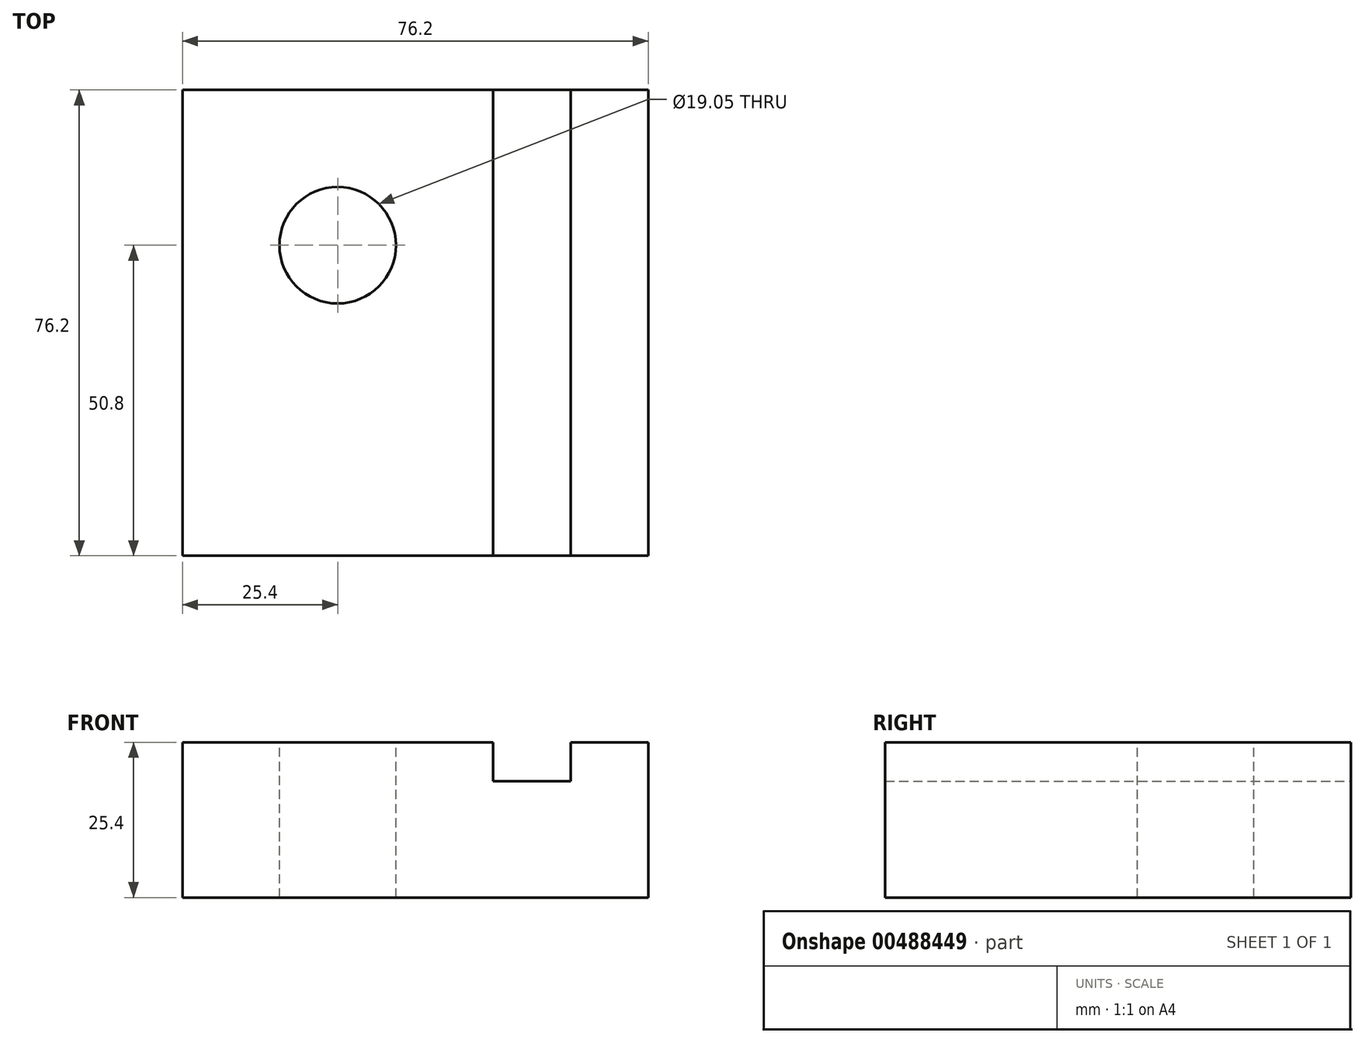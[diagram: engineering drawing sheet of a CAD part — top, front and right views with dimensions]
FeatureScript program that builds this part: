
annotation { "Feature Type Name" : "Feature", "Feature Type Description" : "" }
export const myFeature = defineFeature(function(context is Context, id is Id, definition is map)
    precondition{}
    {
        {
            var Q0;
            Q0=qCreatedBy(makeId("Top.planeOp"),FACE);
            var sketch = newSketch(context, id + "F0", { "sketchPlane" : qUnion([Q0])});
            skLineSegment(sketch, "E0.bottom", {"start": v(38.1, 38.1) * mm, "end": v(-38.1, 38.1) * mm});
            skLineSegment(sketch, "E0.top", {"start": v(38.1, -38.1) * mm, "end": v(-38.1, -38.1) * mm});
            skLineSegment(sketch, "E0.left", {"start": v(38.1, 38.1) * mm, "end": v(38.1, -38.1) * mm});
            skLineSegment(sketch, "E0.right", {"start": v(-38.1, 38.1) * mm, "end": v(-38.1, -38.1) * mm});
            skPoint(sketch, "E0.middle", {"position": v(0, 0) * mm});
            skCircle(sketch, "E1", {"center": v(-12.7, 12.7) * mm, "radius": 9.53 * mm});
            skLineSegment(sketch, "E2", {"start": v(12.7, 38.1) * mm, "end": v(12.7, -38.1) * mm});
            skLineSegment(sketch, "E3", {"start": v(12.7, -38.1) * mm, "end": v(25.4, -38.1) * mm});
            skLineSegment(sketch, "E4", {"start": v(25.4, -38.1) * mm, "end": v(25.4, 38.1) * mm});
            skSolve(sketch);
        }
        {
            var Q0;
            {var subQ0=sQuery(id+"F0.wireOp",EDGE,"E0.left");Q0=makeQuery(id+"F0.imprint","IMPRINT",FACE,{"disambiguationData":[TD([[makeQuery(id+"F0.imprint","IMPRINT",EDGE,{"derivedFrom":subQ0}),-1.0]])]});}
            var Q1;
            {var subQ0=sQuery(id+"F0.wireOp",EDGE,"E0.right");Q1=makeQuery(id+"F0.imprint","IMPRINT",FACE,{"disambiguationData":[TD([[makeQuery(id+"F0.imprint","IMPRINT",EDGE,{"derivedFrom":subQ0}),1.0]])]});}
            var Q2;
            {var subQ0=sQuery(id+"F0.wireOp",EDGE,"E2");Q2=makeQuery(id+"F0.imprint","IMPRINT",FACE,{"disambiguationData":[TD([[makeQuery(id+"F0.imprint","IMPRINT",EDGE,{"derivedFrom":subQ0}),1.0]])]});}
            extrude(context, id + "F1", {"entities" : qUnion([Q0, Q1, Q2]), "oppositeDirection" : true, "depth" : 25.4 * mm, "offsetDistance" : 25.4 * mm});
        }
        {
            var Q0;
            {var subQ0=sQuery(id+"F0.wireOp",EDGE,"E2");Q0=makeQuery(id+"F0.imprint","IMPRINT",FACE,{"disambiguationData":[TD([[makeQuery(id+"F0.imprint","IMPRINT",EDGE,{"derivedFrom":subQ0}),1.0]])]});}
            extrude(context, id + "F2", {"entities" : qUnion([Q0]), "operationType" : NewBodyOperationType.REMOVE, "oppositeDirection" : true, "depth" : 6.35 * mm, "offsetDistance" : 25.4 * mm});
        }
    });
